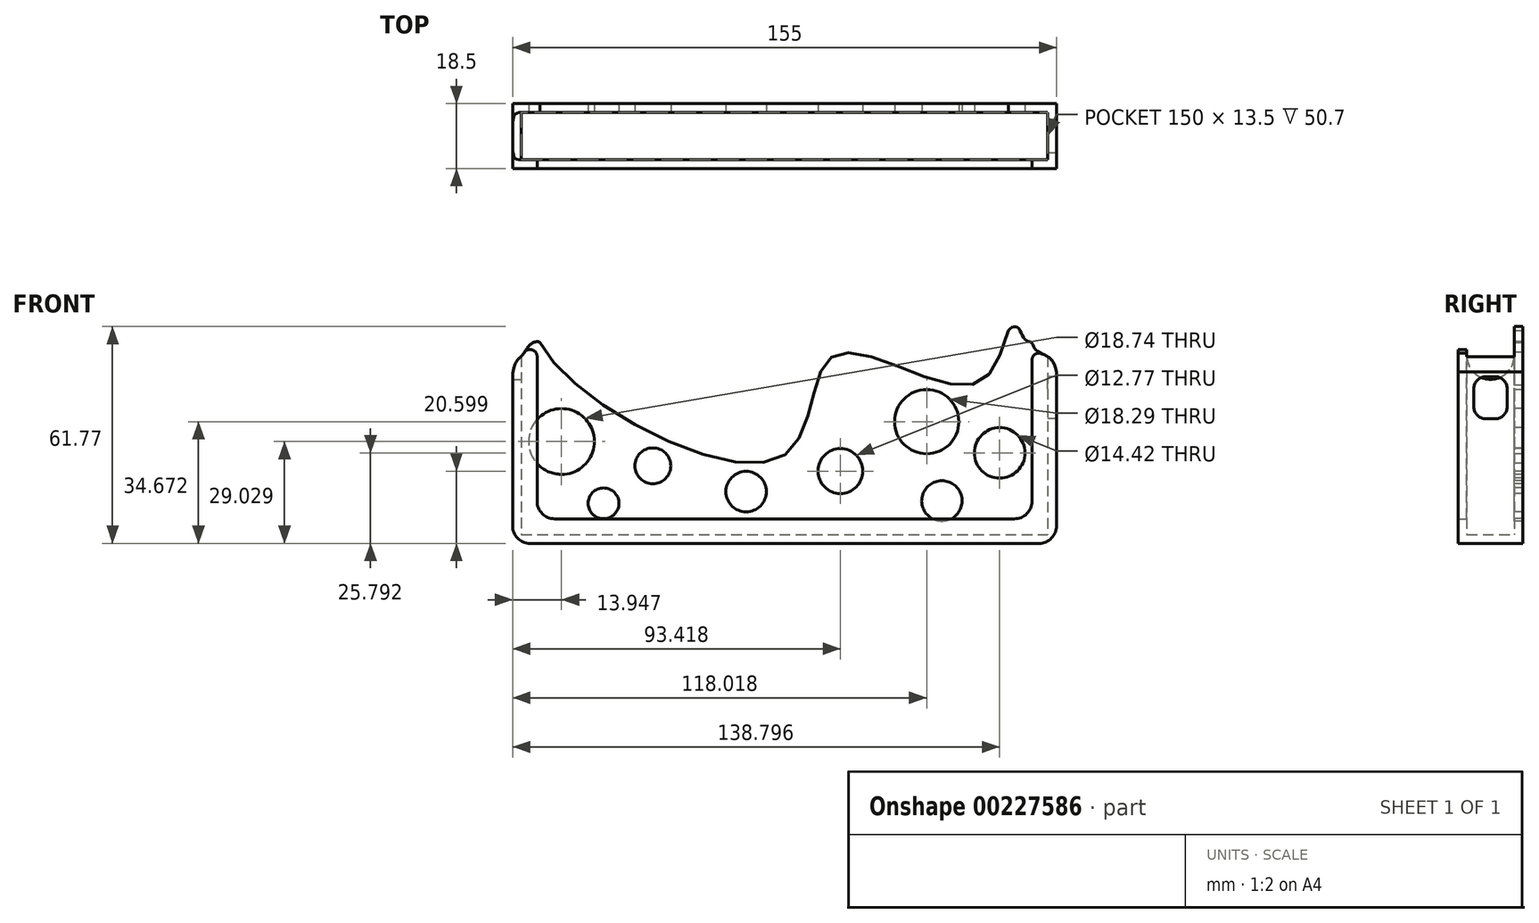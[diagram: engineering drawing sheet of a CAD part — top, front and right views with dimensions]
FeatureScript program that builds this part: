
annotation { "Feature Type Name" : "Feature", "Feature Type Description" : "" }
export const myFeature = defineFeature(function(context is Context, id is Id, definition is map)
    precondition{}
    {
        {
            var Q0;
            Q0=qCreatedBy(makeId("Front.planeOp"),FACE);
            var sketch = newSketch(context, id + "F0", { "sketchPlane" : qUnion([Q0])});
            skLineSegment(sketch, "E0.bottom", {"start": v(-48, 16.82) * mm, "end": v(102, 16.82) * mm});
            skLineSegment(sketch, "E0.top", {"start": v(-48, -58.18) * mm, "end": v(102, -58.18) * mm});
            skLineSegment(sketch, "E0.left", {"start": v(-48, 16.82) * mm, "end": v(-48, -58.18) * mm});
            skLineSegment(sketch, "E0.right", {"start": v(102, 16.82) * mm, "end": v(102, -58.18) * mm});
            skSolve(sketch);
        }
        {
            var Q0;
            Q0=makeQuery(id+"F0.imprint","IMPRINT",FACE,{"disambiguationData":[TD([[makeQuery(id+"F0.imprint","IMPRINT",EDGE,{"derivedFrom":sQuery(id+"F0.wireOp",EDGE,"E0.bottom")}),-1.0]])]});
            extrude(context, id + "F1", {"entities" : qUnion([Q0]), "offsetDistance" : 25 * mm, "depth" : 2.5 * mm});
        }
        {
            var Q0;
            Q0=makeQuery(id+"F1.opExtrude","CAP_FACE",FACE,{"disambiguationData":[OSD([sQuery(id+"F0.wireOp",EDGE,"E0.bottom"),sQuery(id+"F0.wireOp",EDGE,"E0.top"),sQuery(id+"F0.wireOp",EDGE,"E0.left"),sQuery(id+"F0.wireOp",EDGE,"E0.right")])],"isStart":true});
            var sketch = newSketch(context, id + "F2", { "sketchPlane" : qUnion([Q0])});
            skLineSegment(sketch, "E1.bottom", {"start": v(48, 16.82) * mm, "end": v(50.5, 16.82) * mm});
            skLineSegment(sketch, "E1.top", {"start": v(48, -58.18) * mm, "end": v(50.5, -58.18) * mm});
            skLineSegment(sketch, "E1.left", {"start": v(48, 16.82) * mm, "end": v(48, -58.18) * mm});
            skLineSegment(sketch, "E1.right", {"start": v(50.5, 16.82) * mm, "end": v(50.5, -58.18) * mm});
            skLineSegment(sketch, "E2.bottom", {"start": v(48, -58.18) * mm, "end": v(-102, -58.18) * mm});
            skLineSegment(sketch, "E2.top", {"start": v(48, -60.68) * mm, "end": v(-102, -60.68) * mm});
            skLineSegment(sketch, "E2.left", {"start": v(48, -58.18) * mm, "end": v(48, -60.68) * mm});
            skLineSegment(sketch, "E2.right", {"start": v(-102, -58.18) * mm, "end": v(-102, -60.68) * mm});
            skLineSegment(sketch, "E3.bottom", {"start": v(-102, 16.82) * mm, "end": v(-104.5, 16.82) * mm});
            skLineSegment(sketch, "E3.top", {"start": v(-102, -58.18) * mm, "end": v(-104.5, -58.18) * mm});
            skLineSegment(sketch, "E3.left", {"start": v(-102, 16.82) * mm, "end": v(-102, -58.18) * mm});
            skLineSegment(sketch, "E3.right", {"start": v(-104.5, 16.82) * mm, "end": v(-104.5, -58.18) * mm});
            skLineSegment(sketch, "E4", {"start": v(50.5, -58.18) * mm, "end": v(50.5, -60.68) * mm});
            skLineSegment(sketch, "E5", {"start": v(50.5, -60.68) * mm, "end": v(48, -60.68) * mm});
            skLineSegment(sketch, "E6", {"start": v(-102, -60.68) * mm, "end": v(-104.5, -60.68) * mm});
            skLineSegment(sketch, "E7", {"start": v(-104.5, -60.68) * mm, "end": v(-104.5, -58.18) * mm});
            skSolve(sketch);
        }
        {
            var Q0;
            Q0=makeQuery(id+"F2.imprint","IMPRINT",FACE,{"disambiguationData":[TD([[makeQuery(id+"F2.imprint","IMPRINT",EDGE,{"derivedFrom":sQuery(id+"F2.wireOp",EDGE,"E1.bottom")}),-1.0]])]});
            var Q1;
            Q1=makeQuery(id+"F2.imprint","IMPRINT",FACE,{"disambiguationData":[TD([[makeQuery(id+"F2.imprint","IMPRINT",EDGE,{"derivedFrom":sQuery(id+"F2.wireOp",EDGE,"E2.bottom")}),1.0]])]});
            var Q2;
            Q2=makeQuery(id+"F2.imprint","IMPRINT",FACE,{"disambiguationData":[TD([[makeQuery(id+"F2.imprint","IMPRINT",EDGE,{"derivedFrom":sQuery(id+"F2.wireOp",EDGE,"E1.top")}),-1.0]])]});
            var Q3;
            Q3=makeQuery(id+"F2.imprint","IMPRINT",FACE,{"disambiguationData":[TD([[makeQuery(id+"F2.imprint","IMPRINT",EDGE,{"derivedFrom":sQuery(id+"F2.wireOp",EDGE,"E2.right")}),-1.0]])]});
            var Q4;
            Q4=makeQuery(id+"F2.imprint","IMPRINT",FACE,{"disambiguationData":[TD([[makeQuery(id+"F2.imprint","IMPRINT",EDGE,{"derivedFrom":sQuery(id+"F2.wireOp",EDGE,"E3.bottom")}),1.0]])]});
            extrude(context, id + "F3", {"entities" : qUnion([Q0, Q1, Q2, Q3, Q4]), "operationType" : NewBodyOperationType.ADD, "oppositeDirection" : true, "offsetDistance" : 25 * mm, "depth" : 16 * mm});
        }
        {
            var Q0;
            Q0=makeQuery(id+"F3.opExtrude","CAP_FACE",FACE,{"disambiguationData":[OSD([sQuery(id+"F2.wireOp",EDGE,"E1.bottom"),sQuery(id+"F2.wireOp",EDGE,"E1.left"),sQuery(id+"F2.wireOp",EDGE,"E1.right"),sQuery(id+"F2.wireOp",EDGE,"E2.bottom"),sQuery(id+"F2.wireOp",EDGE,"E2.top"),sQuery(id+"F2.wireOp",EDGE,"E3.bottom"),sQuery(id+"F2.wireOp",EDGE,"E3.left"),sQuery(id+"F2.wireOp",EDGE,"E3.right"),sQuery(id+"F2.wireOp",EDGE,"E4"),sQuery(id+"F2.wireOp",EDGE,"E5"),sQuery(id+"F2.wireOp",EDGE,"E6"),sQuery(id+"F2.wireOp",EDGE,"E7")])],"isStart":false});
            var sketch = newSketch(context, id + "F4", { "sketchPlane" : qUnion([Q0])});
            skLineSegment(sketch, "E8", {"start": v(-50.5, 16.82) * mm, "end": v(-43.5, 16.82) * mm});
            skLineSegment(sketch, "E9", {"start": v(-43.5, 16.82) * mm, "end": v(-43.5, -53.68) * mm});
            skLineSegment(sketch, "E10", {"start": v(-43.5, -53.68) * mm, "end": v(97.5, -53.68) * mm});
            skLineSegment(sketch, "E11", {"start": v(97.5, -53.68) * mm, "end": v(97.5, 16.82) * mm});
            skLineSegment(sketch, "E12", {"start": v(97.5, 16.82) * mm, "end": v(104.5, 16.82) * mm});
            skLineSegment(sketch, "E13", {"start": v(104.5, 16.82) * mm, "end": v(104.5, -60.68) * mm});
            skLineSegment(sketch, "E14", {"start": v(104.5, -60.68) * mm, "end": v(-50.5, -60.68) * mm});
            skLineSegment(sketch, "E15", {"start": v(-50.5, -60.68) * mm, "end": v(-50.5, 16.82) * mm});
            skSolve(sketch);
        }
        {
            var Q0;
            {var subQ3=sQuery(id+"F4.wireOp",EDGE,"E9");Q0=makeQuery(id+"F4.imprint","IMPRINT",FACE,{"disambiguationData":[TD([[makeQuery(id+"F4.imprint","IMPRINT",EDGE,{"derivedFrom":subQ3}),-1.0]])]});}
            var Q1;
            {var subQ0=sQuery(id+"F4.wireOp",EDGE,"E13");Q1=makeQuery(id+"F4.imprint","IMPRINT",FACE,{"disambiguationData":[TD([[makeQuery(id+"F4.imprint","IMPRINT",EDGE,{"derivedFrom":subQ0}),1.0]])]});}
            extrude(context, id + "F5", {"entities" : qUnion([Q0, Q1]), "operationType" : NewBodyOperationType.ADD, "depth" : 2.5 * mm});
        }
        {
            var Q0;
            Q0=makeQuery(id+"FYWR5ZG7inD0FhB_1.boolean.opBoolean","MERGE",FACE,{"derivedFrom":[makeQuery(id+"F1.opExtrude","CAP_FACE",FACE,{"disambiguationData":[OSD([sQuery(id+"F0.wireOp",EDGE,"E0.bottom"),sQuery(id+"F0.wireOp",EDGE,"E0.top"),sQuery(id+"F0.wireOp",EDGE,"E0.left"),sQuery(id+"F0.wireOp",EDGE,"E0.right")])],"isStart":false}),makeQuery(id+"FYWR5ZG7inD0FhB_1.opExtrude","SWEPT_FACE",FACE,{"disambiguationData":[OSD([sQuery(id+"Fj1UJKooqcYQIcB_1.wireOp",EDGE,"NuPV9PNT-Ke5e-S10A-4uW3-W4IaAnTDUlg0")])]})]});
            var sketch = newSketch(context, id + "F6", { "sketchPlane" : qUnion([Q0])});
            skFitSpline(sketch, "E16", {"points": [v(-48, 16.82) * mm, v(-37.89, -10.14) * mm, v(27.04, -35.46) * mm, v(41.6, -6.87) * mm, v(82.42, -14.77) * mm, v(102, 16.82) * mm], "startDerivative": vector(38.95, -153.05) * mm, "endDerivative": vector(184.6, 54.57) * mm});
            skSolve(sketch);
        }
        {
            var Q0;
            Q0=makeQuery(id+"F6.imprint","IMPRINT",FACE,{"disambiguationData":[TD([[makeQuery(id+"F6.imprint","IMPRINT",EDGE,{"derivedFrom":sQuery(id+"F6.wireOp",EDGE,"E16")}),1.0]])]});
            extrude(context, id + "F7", {"entities" : qUnion([Q0]), "operationType" : NewBodyOperationType.REMOVE, "oppositeDirection" : true, "depth" : 25 * mm});
        }
        {
            var Q0;
            Q0=makeQuery(id+"FYWR5ZG7inD0FhB_1.boolean.opBoolean","MERGE",FACE,{"derivedFrom":[makeQuery(id+"F1.opExtrude","CAP_FACE",FACE,{"disambiguationData":[OSD([sQuery(id+"F0.wireOp",EDGE,"E0.bottom"),sQuery(id+"F0.wireOp",EDGE,"E0.top"),sQuery(id+"F0.wireOp",EDGE,"E0.left"),sQuery(id+"F0.wireOp",EDGE,"E0.right")])],"isStart":false}),makeQuery(id+"FYWR5ZG7inD0FhB_1.opExtrude","SWEPT_FACE",FACE,{"disambiguationData":[OSD([sQuery(id+"Fj1UJKooqcYQIcB_1.wireOp",EDGE,"NuPV9PNT-Ke5e-S10A-4uW3-W4IaAnTDUlg0")])]})]});
            var sketch = newSketch(context, id + "F8", { "sketchPlane" : qUnion([Q0])});
            skCircle(sketch, "E17", {"center": v(-36.55, -31.65) * mm, "radius": 9.37 * mm});
            skCircle(sketch, "E18", {"center": v(67.52, -26) * mm, "radius": 9.14 * mm});
            skCircle(sketch, "E19", {"center": v(42.92, -40.08) * mm, "radius": 6.39 * mm});
            skCircle(sketch, "E20", {"center": v(71.84, -48.57) * mm, "radius": 5.75 * mm});
            skCircle(sketch, "E21", {"center": v(16.06, -45.93) * mm, "radius": 5.77 * mm});
            skCircle(sketch, "E22", {"center": v(-24.55, -49.27) * mm, "radius": 4.38 * mm});
            skCircle(sketch, "E23", {"center": v(-10.52, -38.58) * mm, "radius": 5.11 * mm});
            skCircle(sketch, "E24", {"center": v(88.3, -34.89) * mm, "radius": 7.2 * mm});
            skSolve(sketch);
        }
        {
            var Q0;
            Q0=makeQuery(id+"F8.imprint","IMPRINT",FACE,{"disambiguationData":[TD([[makeQuery(id+"F8.imprint","IMPRINT",EDGE,{"derivedFrom":sQuery(id+"F8.wireOp",EDGE,"E23")}),1.0]])]});
            var Q1;
            Q1=makeQuery(id+"F8.imprint","IMPRINT",FACE,{"disambiguationData":[TD([[makeQuery(id+"F8.imprint","IMPRINT",EDGE,{"derivedFrom":sQuery(id+"F8.wireOp",EDGE,"E22")}),1.0]])]});
            var Q2;
            Q2=makeQuery(id+"F8.imprint","IMPRINT",FACE,{"disambiguationData":[TD([[makeQuery(id+"F8.imprint","IMPRINT",EDGE,{"derivedFrom":sQuery(id+"F8.wireOp",EDGE,"E17")}),1.0]])]});
            var Q3;
            Q3=makeQuery(id+"F8.imprint","IMPRINT",FACE,{"disambiguationData":[TD([[makeQuery(id+"F8.imprint","IMPRINT",EDGE,{"derivedFrom":sQuery(id+"F8.wireOp",EDGE,"E21")}),1.0]])]});
            var Q4;
            Q4=makeQuery(id+"F8.imprint","IMPRINT",FACE,{"disambiguationData":[TD([[makeQuery(id+"F8.imprint","IMPRINT",EDGE,{"derivedFrom":sQuery(id+"F8.wireOp",EDGE,"E19")}),1.0]])]});
            var Q5;
            Q5=makeQuery(id+"F8.imprint","IMPRINT",FACE,{"disambiguationData":[TD([[makeQuery(id+"F8.imprint","IMPRINT",EDGE,{"derivedFrom":sQuery(id+"F8.wireOp",EDGE,"E18")}),1.0]])]});
            var Q6;
            Q6=makeQuery(id+"F8.imprint","IMPRINT",FACE,{"disambiguationData":[TD([[makeQuery(id+"F8.imprint","IMPRINT",EDGE,{"derivedFrom":sQuery(id+"F8.wireOp",EDGE,"E20")}),1.0]])]});
            var Q7;
            Q7=makeQuery(id+"F8.imprint","IMPRINT",FACE,{"disambiguationData":[TD([[makeQuery(id+"F8.imprint","IMPRINT",EDGE,{"derivedFrom":sQuery(id+"F8.wireOp",EDGE,"E24")}),1.0]])]});
            extrude(context, id + "F9", {"entities" : qUnion([Q0, Q1, Q2, Q3, Q4, Q5, Q6, Q7]), "operationType" : NewBodyOperationType.REMOVE, "oppositeDirection" : true, "offsetDistance" : 25 * mm, "depth" : 25 * mm});
        }
        {
            var Q0;
            Q0=makeQuery(id+"F5.opExtrude","SWEPT_EDGE",EDGE,{"disambiguationData":[OSD([sQuery(id+"F4.wireOp",EDGE,"E8"),sQuery(id+"F4.wireOp",EDGE,"E9")])]});
            var Q1;
            Q1=makeQuery(id+"F5.opExtrude","SWEPT_EDGE",EDGE,{"disambiguationData":[OSD([sQuery(id+"F4.wireOp",EDGE,"E11"),sQuery(id+"F4.wireOp",EDGE,"E12")])]});
            fillet(context, id + "F10", {"entities" : qUnion([Q0, Q1]), "radius" : 2.5 * mm, "tangentPropagation" : true, "allowEdgeOverflow" : false});
        }
        {
            var Q0;
            Q0=makeQuery(id+"F3.boolean.opBoolean","MERGE",FACE,{"derivedFrom":[makeQuery(id+"F1.opExtrude","CAP_FACE",FACE,{"disambiguationData":[OSD([sQuery(id+"F0.wireOp",EDGE,"E0.bottom"),sQuery(id+"F0.wireOp",EDGE,"E0.top"),sQuery(id+"F0.wireOp",EDGE,"E0.left"),sQuery(id+"F0.wireOp",EDGE,"E0.right")])],"isStart":true}),makeQuery(id+"F3.opExtrude","CAP_FACE",FACE,{"disambiguationData":[OSD([sQuery(id+"F2.wireOp",EDGE,"E1.bottom"),sQuery(id+"F2.wireOp",EDGE,"E1.left"),sQuery(id+"F2.wireOp",EDGE,"E1.right"),sQuery(id+"F2.wireOp",EDGE,"E2.bottom"),sQuery(id+"F2.wireOp",EDGE,"E2.top"),sQuery(id+"F2.wireOp",EDGE,"E3.bottom"),sQuery(id+"F2.wireOp",EDGE,"E3.left"),sQuery(id+"F2.wireOp",EDGE,"E3.right"),sQuery(id+"F2.wireOp",EDGE,"E4"),sQuery(id+"F2.wireOp",EDGE,"E5"),sQuery(id+"F2.wireOp",EDGE,"E6"),sQuery(id+"F2.wireOp",EDGE,"E7")])],"isStart":true})]});
            var sketch = newSketch(context, id + "F11", { "sketchPlane" : qUnion([Q0])});
            skFitSpline(sketch, "E25", {"points": [v(-89.88, -2.95) * mm, v(-90.84, 0) * mm, v(-92.68, 1.09) * mm, v(-94.09, 0) * mm, v(-95.55, -2.6) * mm, v(-97.47, -3.57) * mm, v(-98.26, -5.22) * mm, v(-100.56, -6.74) * mm, v(-104.5, -11.81) * mm], "startDerivative": vector(-10.68, 32.26) * mm, "endDerivative": vector(-10.35, -56.8) * mm});
            skFitSpline(sketch, "E26", {"points": [v(38.46, -9.49) * mm, v(40.7, -6.61) * mm, v(42.65, -3.46) * mm, v(44.54, -3.45) * mm, v(46.1, -4.75) * mm, v(47.82, -7.17) * mm, v(50.5, -14.49) * mm], "startDerivative": vector(15.07, 14.79) * mm, "endDerivative": vector(0, -66.18) * mm});
            skLineSegment(sketch, "E27", {"start": v(-104.5, -11.81) * mm, "end": v(-104.5, 23.98) * mm});
            skLineSegment(sketch, "E28", {"start": v(-104.5, 23.98) * mm, "end": v(-89.88, 23.98) * mm});
            skLineSegment(sketch, "E29", {"start": v(-89.88, 23.98) * mm, "end": v(-89.88, -2.95) * mm});
            skLineSegment(sketch, "E30", {"start": v(38.46, -9.49) * mm, "end": v(39.32, -8.64) * mm});
            skLineSegment(sketch, "E31", {"start": v(50.5, -14.49) * mm, "end": v(50.5, 30.55) * mm});
            skLineSegment(sketch, "E32", {"start": v(50.5, 30.55) * mm, "end": v(38.46, 30.55) * mm});
            skLineSegment(sketch, "E33", {"start": v(38.46, 30.55) * mm, "end": v(38.46, -9.49) * mm});
            skSolve(sketch);
        }
        {
            var Q0;
            {var subQ0=sQuery(id+"F11.wireOp",EDGE,"E27");var subQ1=sQuery(id+"F11.wireOp",EDGE,"E25");var subQ2=sQuery(id+"F2.wireOp",EDGE,"E7");var subQ3=sQuery(id+"F2.wireOp",EDGE,"E3.right");var subQ4=makeQuery(id+"F11.imprint","INTERSECT",VERTEX,{"derivedFrom":[makeQuery(id+"F3.opExtrude","CAP_EDGE",EDGE,{"disambiguationData":[OSD([subQ3,subQ2])],"isStart":true}),subQ1,subQ0]});Q0=makeQuery(id+"F11.imprint","IMPRINT",FACE,{"disambiguationData":[TD([[makeQuery(id+"F11.imprint","IMPRINT",EDGE,{"disambiguationData":[TD([[subQ4,1.0]])],"derivedFrom":subQ1}),-1.0]])]});}
            var Q1;
            {var subQ0=sQuery(id+"F11.wireOp",EDGE,"E31");var subQ1=sQuery(id+"F11.wireOp",EDGE,"E26");var subQ2=sQuery(id+"F2.wireOp",EDGE,"E4");var subQ3=sQuery(id+"F2.wireOp",EDGE,"E1.right");var subQ4=makeQuery(id+"F11.imprint","INTERSECT",VERTEX,{"derivedFrom":[makeQuery(id+"F3.opExtrude","CAP_EDGE",EDGE,{"disambiguationData":[OSD([subQ3,subQ2])],"isStart":true}),subQ1,subQ0]});Q1=makeQuery(id+"F11.imprint","IMPRINT",FACE,{"disambiguationData":[TD([[makeQuery(id+"F11.imprint","IMPRINT",EDGE,{"disambiguationData":[TD([[subQ4,1.0]])],"derivedFrom":subQ1}),1.0]])]});}
            var Q2;
            {var subQ1=sQuery(id+"F11.wireOp",EDGE,"E32");Q2=makeQuery(id+"F11.imprint","IMPRINT",FACE,{"disambiguationData":[TD([[makeQuery(id+"F11.imprint","IMPRINT",EDGE,{"derivedFrom":subQ1}),1.0]])]});}
            var Q3;
            {var subQ1=sQuery(id+"F11.wireOp",EDGE,"E28");Q3=makeQuery(id+"F11.imprint","IMPRINT",FACE,{"disambiguationData":[TD([[makeQuery(id+"F11.imprint","IMPRINT",EDGE,{"derivedFrom":subQ1}),-1.0]])]});}
            extrude(context, id + "F12", {"entities" : qUnion([Q0, Q1, Q2, Q3]), "operationType" : NewBodyOperationType.REMOVE, "endBound" : BoundingType.THROUGH_ALL, "oppositeDirection" : true, "depth" : 25 * mm});
        }
        {
            var Q0;
            Q0=makeQuery(id+"F12.boolean.opBoolean","INTERSECT",EDGE,{"derivedFrom":[makeQuery(id+"F5.opExtrude","SWEPT_FACE",FACE,{"disambiguationData":[OSD([sQuery(id+"F4.wireOp",EDGE,"E9")])]}),makeQuery(id+"F12.opExtrude","SWEPT_FACE",FACE,{"disambiguationData":[OSD([sQuery(id+"F11.wireOp",EDGE,"E26")])]})]});
            fillet(context, id + "F13", {"entities" : qUnion([Q0]), "radius" : 2 * mm, "tangentPropagation" : true, "allowEdgeOverflow" : false});
        }
        {
            var Q0;
            Q0=makeQuery(id+"F12.boolean.opBoolean","INTERSECT",EDGE,{"derivedFrom":[makeQuery(id+"F5.opExtrude","SWEPT_FACE",FACE,{"disambiguationData":[OSD([sQuery(id+"F4.wireOp",EDGE,"E11")])]}),makeQuery(id+"F12.opExtrude","SWEPT_FACE",FACE,{"disambiguationData":[OSD([sQuery(id+"F11.wireOp",EDGE,"E25")])]})]});
            fillet(context, id + "F14", {"entities" : qUnion([Q0]), "radius" : 2 * mm, "tangentPropagation" : true, "allowEdgeOverflow" : false});
        }
        {
            var Q0;
            Q0=makeQuery(id+"F3.opExtrude","SWEPT_FACE",FACE,{"disambiguationData":[OSD([sQuery(id+"F2.wireOp",EDGE,"E1.left")])]});
            var sketch = newSketch(context, id + "F15", { "sketchPlane" : qUnion([Q0])});
            skCircle(sketch, "E34", {"center": v(-9.25, -7.18) * mm, "radius": 6.75 * mm});
            skSolve(sketch);
        }
        {
            var Q0;
            {var subQ0=sQuery(id+"F15.wireOp",EDGE,"E34");var subQ4=makeQuery(id+"F15.imprint","INTERSECT",VERTEX,{"derivedFrom":[makeQuery(id+"F1.opExtrude","CAP_EDGE",EDGE,{"disambiguationData":[OSD([sQuery(id+"F0.wireOp",EDGE,"E0.left")])],"isStart":false}),subQ0]});Q0=makeQuery(id+"F15.imprint","IMPRINT",FACE,{"disambiguationData":[TD([[makeQuery(id+"F15.imprint","IMPRINT",EDGE,{"disambiguationData":[TD([[subQ4,1.0]])],"derivedFrom":subQ0}),1.0]])]});}
            extrude(context, id + "F16", {"entities" : qUnion([Q0]), "operationType" : NewBodyOperationType.REMOVE, "oppositeDirection" : true, "depth" : 25 * mm, "offsetDistance" : 25 * mm});
        }
        {
            var Q0;
            Q0=makeQuery(id+"F3.opExtrude","SWEPT_FACE",FACE,{"disambiguationData":[OSD([sQuery(id+"F2.wireOp",EDGE,"E3.left")])]});
            var sketch = newSketch(context, id + "F17", { "sketchPlane" : qUnion([Q0])});
            skLineSegment(sketch, "E35.bottom", {"start": v(4.5, -13.18) * mm, "end": v(14, -13.18) * mm});
            skLineSegment(sketch, "E35.top", {"start": v(4.5, -25.18) * mm, "end": v(14, -25.18) * mm});
            skLineSegment(sketch, "E35.left", {"start": v(4.5, -13.18) * mm, "end": v(4.5, -25.18) * mm});
            skLineSegment(sketch, "E35.right", {"start": v(14, -13.18) * mm, "end": v(14, -25.18) * mm});
            skSolve(sketch);
        }
        {
            var Q0;
            Q0=makeQuery(id+"F17.imprint","IMPRINT",FACE,{"disambiguationData":[TD([[makeQuery(id+"F17.imprint","IMPRINT",EDGE,{"derivedFrom":sQuery(id+"F17.wireOp",EDGE,"E35.bottom")}),-1.0]])]});
            extrude(context, id + "F18", {"entities" : qUnion([Q0]), "operationType" : NewBodyOperationType.REMOVE, "oppositeDirection" : true, "depth" : 25 * mm, "offsetDistance" : 25 * mm});
        }
        {
            var Q0;
            Q0=makeQuery(id+"F18.boolean.opBoolean","COPY",EDGE,{"derivedFrom":makeQuery(id+"F18.opExtrude","SWEPT_EDGE",EDGE,{"disambiguationData":[OSD([sQuery(id+"F17.wireOp",EDGE,"E35.top"),sQuery(id+"F17.wireOp",EDGE,"E35.left")])]})});
            var Q1;
            Q1=makeQuery(id+"F18.boolean.opBoolean","COPY",EDGE,{"derivedFrom":makeQuery(id+"F18.opExtrude","SWEPT_EDGE",EDGE,{"disambiguationData":[OSD([sQuery(id+"F17.wireOp",EDGE,"E35.top"),sQuery(id+"F17.wireOp",EDGE,"E35.right")])]})});
            var Q2;
            Q2=makeQuery(id+"F18.boolean.opBoolean","COPY",EDGE,{"derivedFrom":makeQuery(id+"F18.opExtrude","SWEPT_EDGE",EDGE,{"disambiguationData":[OSD([sQuery(id+"F17.wireOp",EDGE,"E35.bottom"),sQuery(id+"F17.wireOp",EDGE,"E35.left")])]})});
            var Q3;
            Q3=makeQuery(id+"F18.boolean.opBoolean","COPY",EDGE,{"derivedFrom":makeQuery(id+"F18.opExtrude","SWEPT_EDGE",EDGE,{"disambiguationData":[OSD([sQuery(id+"F17.wireOp",EDGE,"E35.bottom"),sQuery(id+"F17.wireOp",EDGE,"E35.right")])]})});
            fillet(context, id + "F19", {"entities" : qUnion([Q0, Q1, Q2, Q3]), "radius" : 3.4 * mm, "tangentPropagation" : true, "allowEdgeOverflow" : false});
        }
        {
            var Q0;
            Q0=makeQuery(id+"F5.opExtrude","SWEPT_EDGE",EDGE,{"disambiguationData":[OSD([sQuery(id+"F4.wireOp",EDGE,"E9"),sQuery(id+"F4.wireOp",EDGE,"E10")])]});
            var Q1;
            Q1=makeQuery(id+"F5.opExtrude","SWEPT_EDGE",EDGE,{"disambiguationData":[OSD([sQuery(id+"F4.wireOp",EDGE,"E10"),sQuery(id+"F4.wireOp",EDGE,"E11")])]});
            fillet(context, id + "F20", {"entities" : qUnion([Q0, Q1]), "radius" : 5 * mm, "tangentPropagation" : true, "allowEdgeOverflow" : false});
        }
        {
            var Q0;
            Q0=makeQuery(id+"F5.boolean.opBoolean","MERGE",EDGE,{"derivedFrom":[makeQuery(id+"F3.opExtrude","SWEPT_EDGE",EDGE,{"disambiguationData":[OSD([sQuery(id+"F2.wireOp",EDGE,"E4"),sQuery(id+"F2.wireOp",EDGE,"E5")])]}),makeQuery(id+"F5.opExtrude","SWEPT_EDGE",EDGE,{"disambiguationData":[OSD([sQuery(id+"F4.wireOp",EDGE,"E14"),sQuery(id+"F4.wireOp",EDGE,"E15")])]})]});
            var Q1;
            Q1=makeQuery(id+"F5.boolean.opBoolean","MERGE",EDGE,{"derivedFrom":[makeQuery(id+"F3.opExtrude","SWEPT_EDGE",EDGE,{"disambiguationData":[OSD([sQuery(id+"F2.wireOp",EDGE,"E6"),sQuery(id+"F2.wireOp",EDGE,"E7")])]}),makeQuery(id+"F5.opExtrude","SWEPT_EDGE",EDGE,{"disambiguationData":[OSD([sQuery(id+"F4.wireOp",EDGE,"E13"),sQuery(id+"F4.wireOp",EDGE,"E14")])]})]});
            fillet(context, id + "F21", {"entities" : qUnion([Q0, Q1]), "radius" : 5 * mm, "tangentPropagation" : true, "allowEdgeOverflow" : false});
        }
    });
